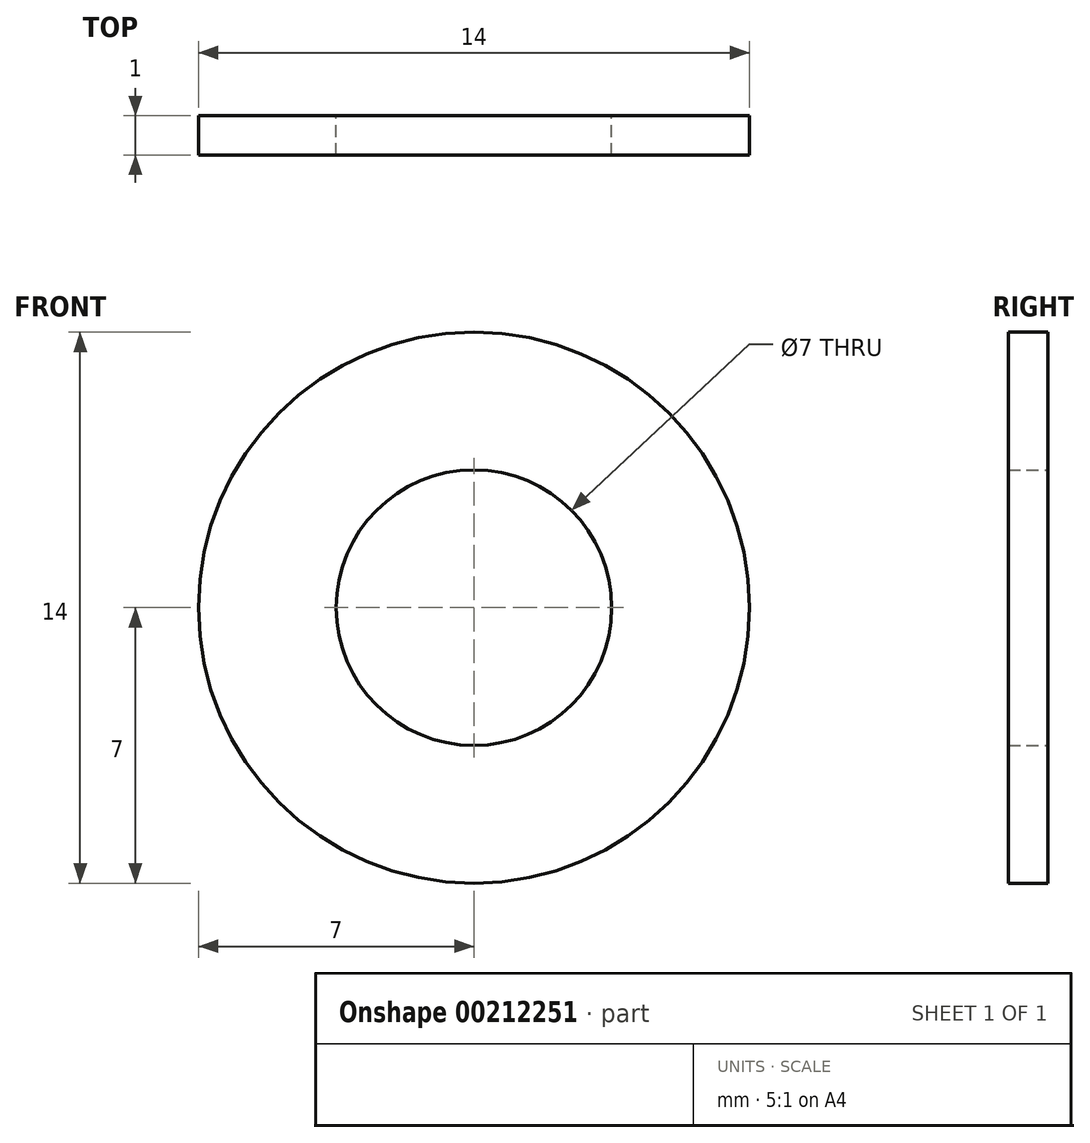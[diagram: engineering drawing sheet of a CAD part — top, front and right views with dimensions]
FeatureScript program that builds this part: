
annotation { "Feature Type Name" : "Feature", "Feature Type Description" : "" }
export const myFeature = defineFeature(function(context is Context, id is Id, definition is map)
    precondition{}
    {
        {
            var Q0;
            Q0=qCreatedBy(makeId("Front.planeOp"),FACE);
            var sketch = newSketch(context, id + "F1", { "sketchPlane" : qUnion([Q0])});
            skCircle(sketch, "E0", {"center": v(0, 0) * mm, "radius": 7 * mm});
            skCircle(sketch, "E1", {"center": v(0, 0) * mm, "radius": 3.5 * mm});
            skSolve(sketch);
        }
        {
            var Q0;
            Q0 = qSketchRegion(id + "F1", true);
            extrude(context, id + "F0", {"entities" : qUnion([Q0]), "depth" : 1 * mm});
        }
    });
